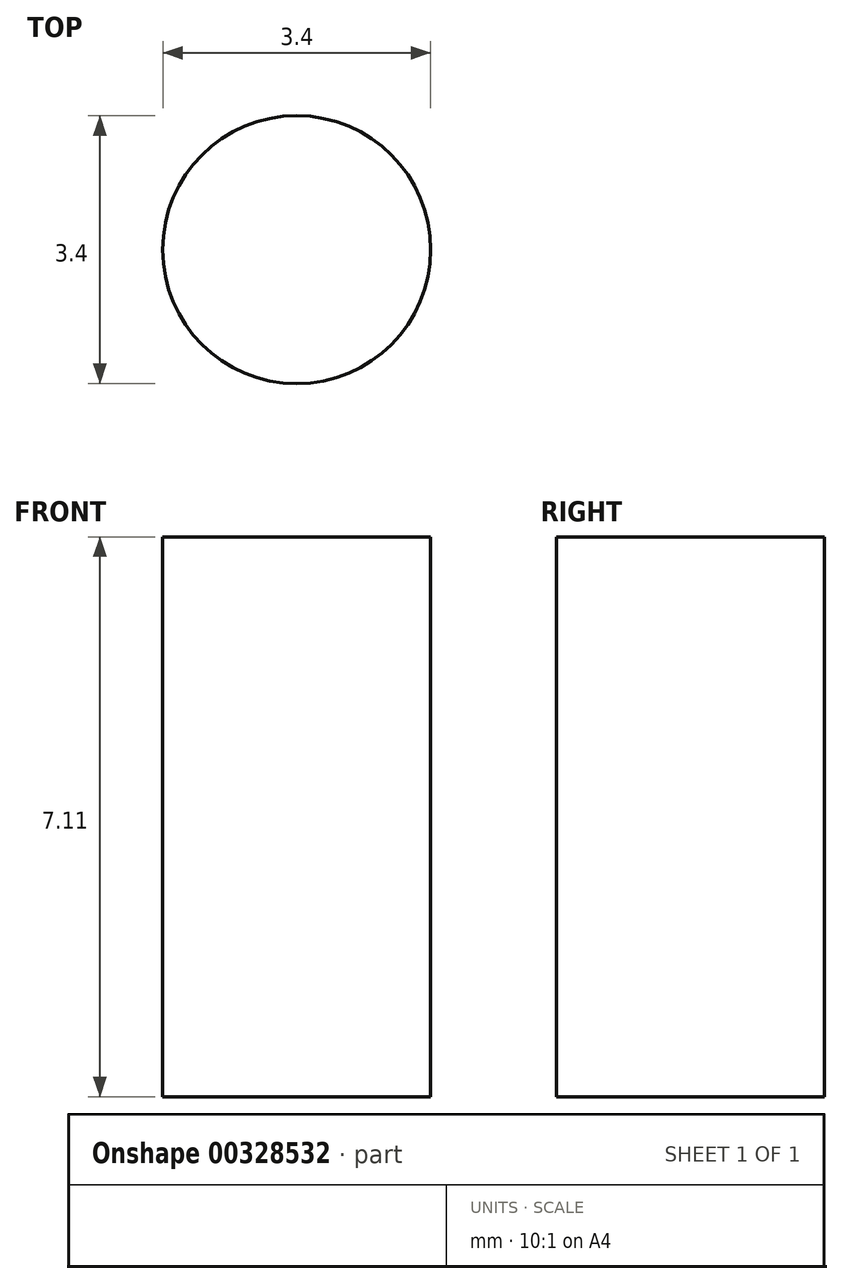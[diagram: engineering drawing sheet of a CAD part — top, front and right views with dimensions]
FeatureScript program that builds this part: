
annotation { "Feature Type Name" : "Feature", "Feature Type Description" : "" }
export const myFeature = defineFeature(function(context is Context, id is Id, definition is map)
    precondition{}
    {
        {
            var Q0;
            Q0=qCreatedBy(makeId("Top.planeOp"),FACE);
            var sketch = newSketch(context, id + "F0", { "sketchPlane" : qUnion([Q0])});
            skCircle(sketch, "E0", {"center": v(0, 0) * mm, "radius": 1.7 * mm});
            skSolve(sketch);
        }
        {
            var Q0;
            Q0=makeQuery(id+"F0.imprint","IMPRINT",FACE,{"disambiguationData":[TD([[makeQuery(id+"F0.imprint","IMPRINT",EDGE,{"derivedFrom":sQuery(id+"F0.wireOp",EDGE,"E0")}),1.0]])]});
            extrude(context, id + "F1", {"entities" : qUnion([Q0]), "depth" : 7.11 * mm});
        }
    });
